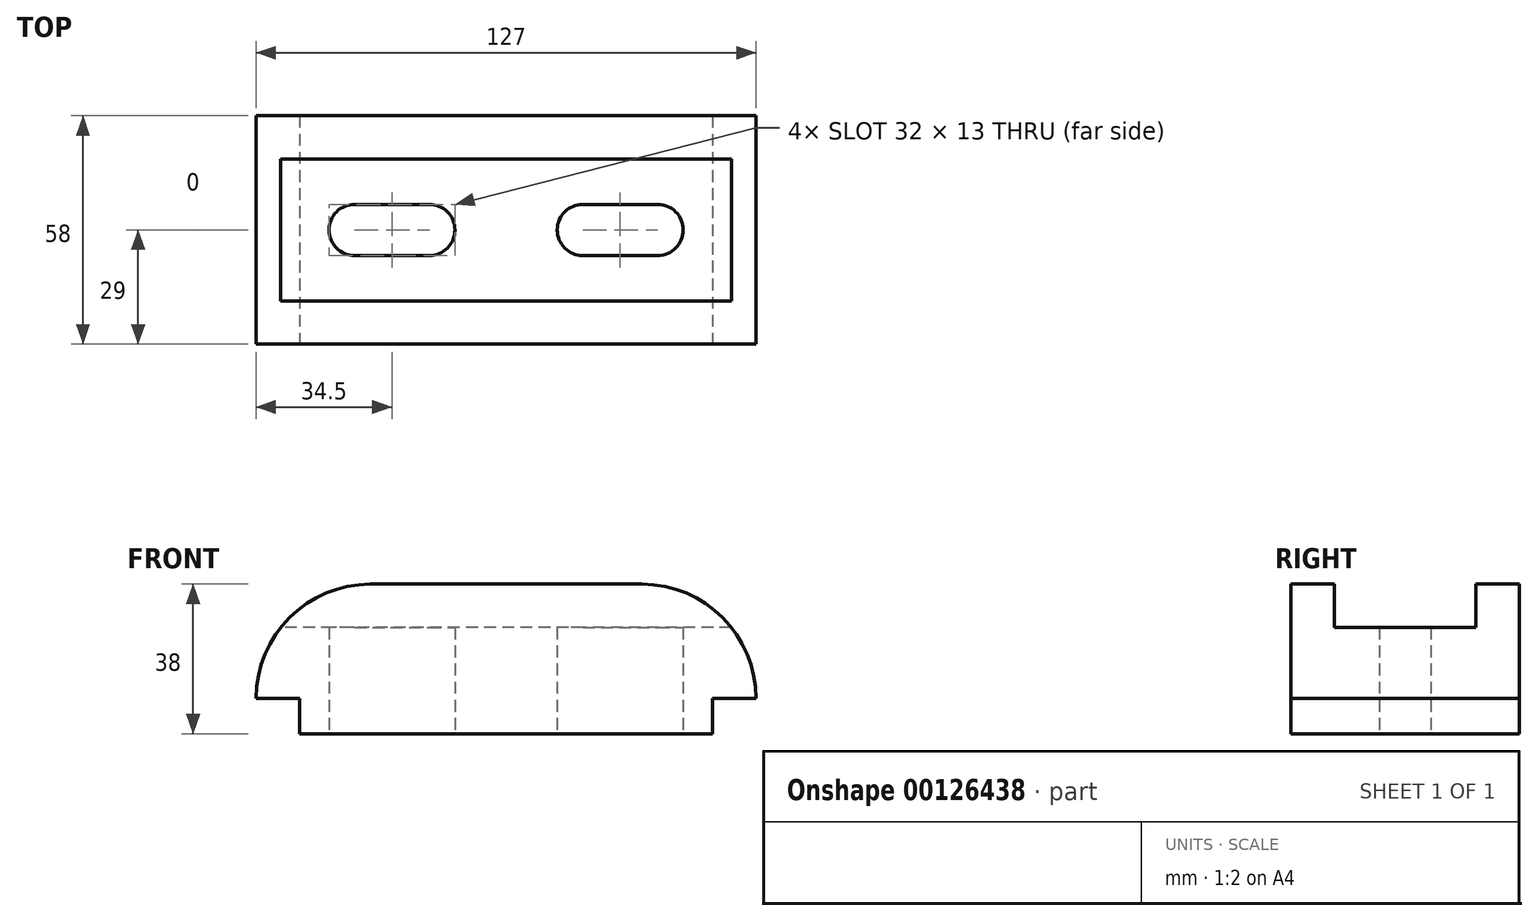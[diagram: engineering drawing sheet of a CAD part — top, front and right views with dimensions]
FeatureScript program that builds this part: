
annotation { "Feature Type Name" : "Feature", "Feature Type Description" : "" }
export const myFeature = defineFeature(function(context is Context, id is Id, definition is map)
    precondition{}
    {
        {
            var Q0;
            Q0=qCreatedBy(makeId("Front.planeOp"),FACE);
            var sketch = newSketch(context, id + "F0", { "sketchPlane" : qUnion([Q0])});
            skLineSegment(sketch, "E0", {"start": v(0, 0) * mm, "end": v(-52.5, 0) * mm});
            skLineSegment(sketch, "E1", {"start": v(0, 0) * mm, "end": v(52.5, 0) * mm});
            skLineSegment(sketch, "E2", {"start": v(-52.5, 0) * mm, "end": v(-52.5, 9) * mm});
            skLineSegment(sketch, "E3", {"start": v(-52.5, 9) * mm, "end": v(-63.5, 9) * mm});
            skLineSegment(sketch, "E4", {"start": v(52.5, 0) * mm, "end": v(52.5, 9) * mm});
            skLineSegment(sketch, "E5", {"start": v(52.5, 9) * mm, "end": v(63.5, 9) * mm});
            skLineSegment(sketch, "E6", {"start": v(-63.5, 9) * mm, "end": v(-63.5, 38) * mm});
            skLineSegment(sketch, "E7", {"start": v(63.5, 9) * mm, "end": v(63.5, 38) * mm});
            skLineSegment(sketch, "E8", {"start": v(63.5, 38) * mm, "end": v(-63.5, 38) * mm});
            skSolve(sketch);
        }
        {
            var Q0;
            Q0=qSketchRegion(id+"F0",true);
            extrude(context, id + "F1", {"entities" : qUnion([Q0]), "endBound" : BoundingType.SYMMETRIC, "oppositeDirection" : true, "depth" : 58 * mm});
        }
        {
            var Q0;
            Q0=makeQuery(id+"F1.opExtrude","SWEPT_EDGE",EDGE,{"disambiguationData":[OSD([sQuery(id+"F0.wireOp",EDGE,"E7"),sQuery(id+"F0.wireOp",EDGE,"E8")])]});
            var Q1;
            Q1=makeQuery(id+"F1.opExtrude","SWEPT_EDGE",EDGE,{"disambiguationData":[OSD([sQuery(id+"F0.wireOp",EDGE,"E6"),sQuery(id+"F0.wireOp",EDGE,"E8")])]});
            fillet(context, id + "F2", {"entities" : qUnion([Q0, Q1]), "radius" : 29 * mm, "tangentPropagation" : true, "allowEdgeOverflow" : false});
        }
        {
            var Q0;
            Q0=qCreatedBy(makeId("Top.planeOp"),FACE);
            var sketch = newSketch(context, id + "F3", { "sketchPlane" : qUnion([Q0])});
            skLineSegment(sketch, "E9", {"start": v(0, 0) * mm, "end": v(-19.5, 0) * mm, "construction": true});
            skLineSegment(sketch, "E10", {"start": v(-19.5, 0) * mm, "end": v(-38.5, 0) * mm, "construction": true});
            skLineSegment(sketch, "E11", {"start": v(0, 0) * mm, "end": v(19.5, 0) * mm, "construction": true});
            skLineSegment(sketch, "E12", {"start": v(19.5, 0) * mm, "end": v(38.5, 0) * mm, "construction": true});
            skArc(sketch, "E13", {"start": v(-38.5, 6.5) * mm, "mid": v(-45, 0) * mm, "end": v(-38.5, -6.5) * mm});
            skArc(sketch, "E14", {"start": v(-19.5, -6.5) * mm, "mid": v(-13, 0) * mm, "end": v(-19.5, 6.5) * mm});
            skArc(sketch, "E15", {"start": v(19.5, 6.5) * mm, "mid": v(13, 0) * mm, "end": v(19.5, -6.5) * mm});
            skArc(sketch, "E16", {"start": v(38.5, -6.5) * mm, "mid": v(45, 0) * mm, "end": v(38.5, 6.5) * mm});
            skLineSegment(sketch, "E17", {"start": v(-38.5, -6.5) * mm, "end": v(-19.5, -6.5) * mm});
            skLineSegment(sketch, "E18", {"start": v(-38.5, 6.5) * mm, "end": v(-19.5, 6.5) * mm});
            skLineSegment(sketch, "E19", {"start": v(19.5, -6.5) * mm, "end": v(38.5, -6.5) * mm});
            skLineSegment(sketch, "E20", {"start": v(19.5, 6.5) * mm, "end": v(38.5, 6.5) * mm});
            skSolve(sketch);
        }
        {
            var Q0;
            Q0=makeQuery(id+"F3.imprint","IMPRINT",FACE,{"disambiguationData":[TD([[makeQuery(id+"F3.imprint","IMPRINT",EDGE,{"derivedFrom":sQuery(id+"F3.wireOp",EDGE,"E13")}),1.0]])]});
            var Q1;
            Q1=makeQuery(id+"F3.imprint","IMPRINT",FACE,{"disambiguationData":[TD([[makeQuery(id+"F3.imprint","IMPRINT",EDGE,{"derivedFrom":sQuery(id+"F3.wireOp",EDGE,"E15")}),1.0]])]});
            var Q2;
            Q2=makeQuery(id+"F1.opExtrude","SWEPT_FACE",FACE,{"disambiguationData":[OSD([sQuery(id+"F0.wireOp",EDGE,"E8")])]});
            extrude(context, id + "F4", {"entities" : qUnion([Q0, Q1]), "operationType" : NewBodyOperationType.REMOVE, "endBound" : BoundingType.UP_TO_SURFACE, "endBoundEntityFace" : qUnion([Q2]), "depth" : 25 * mm});
        }
        {
            var Q0;
            Q0=qCreatedBy(makeId("Front.planeOp"),FACE);
            var sketch = newSketch(context, id + "F5", { "sketchPlane" : qUnion([Q0])});
            skLineSegment(sketch, "E21", {"start": v(0, 0) * mm, "end": v(0, 38) * mm, "construction": true});
            skLineSegment(sketch, "E22", {"start": v(0, 38) * mm, "end": v(63.5, 38) * mm});
            skLineSegment(sketch, "E23", {"start": v(0, 38) * mm, "end": v(-63.5, 38) * mm});
            skLineSegment(sketch, "E24", {"start": v(-63.5, 38) * mm, "end": v(-63.5, 27) * mm});
            skLineSegment(sketch, "E25", {"start": v(63.5, 38) * mm, "end": v(63.5, 27) * mm});
            skLineSegment(sketch, "E26", {"start": v(63.5, 27) * mm, "end": v(-63.5, 27) * mm});
            skSolve(sketch);
        }
        {
            var Q0;
            Q0=qSketchRegion(id+"F5",true);
            extrude(context, id + "F6", {"entities" : qUnion([Q0]), "operationType" : NewBodyOperationType.REMOVE, "endBound" : BoundingType.SYMMETRIC, "oppositeDirection" : true, "depth" : 36 * mm});
        }
    });
